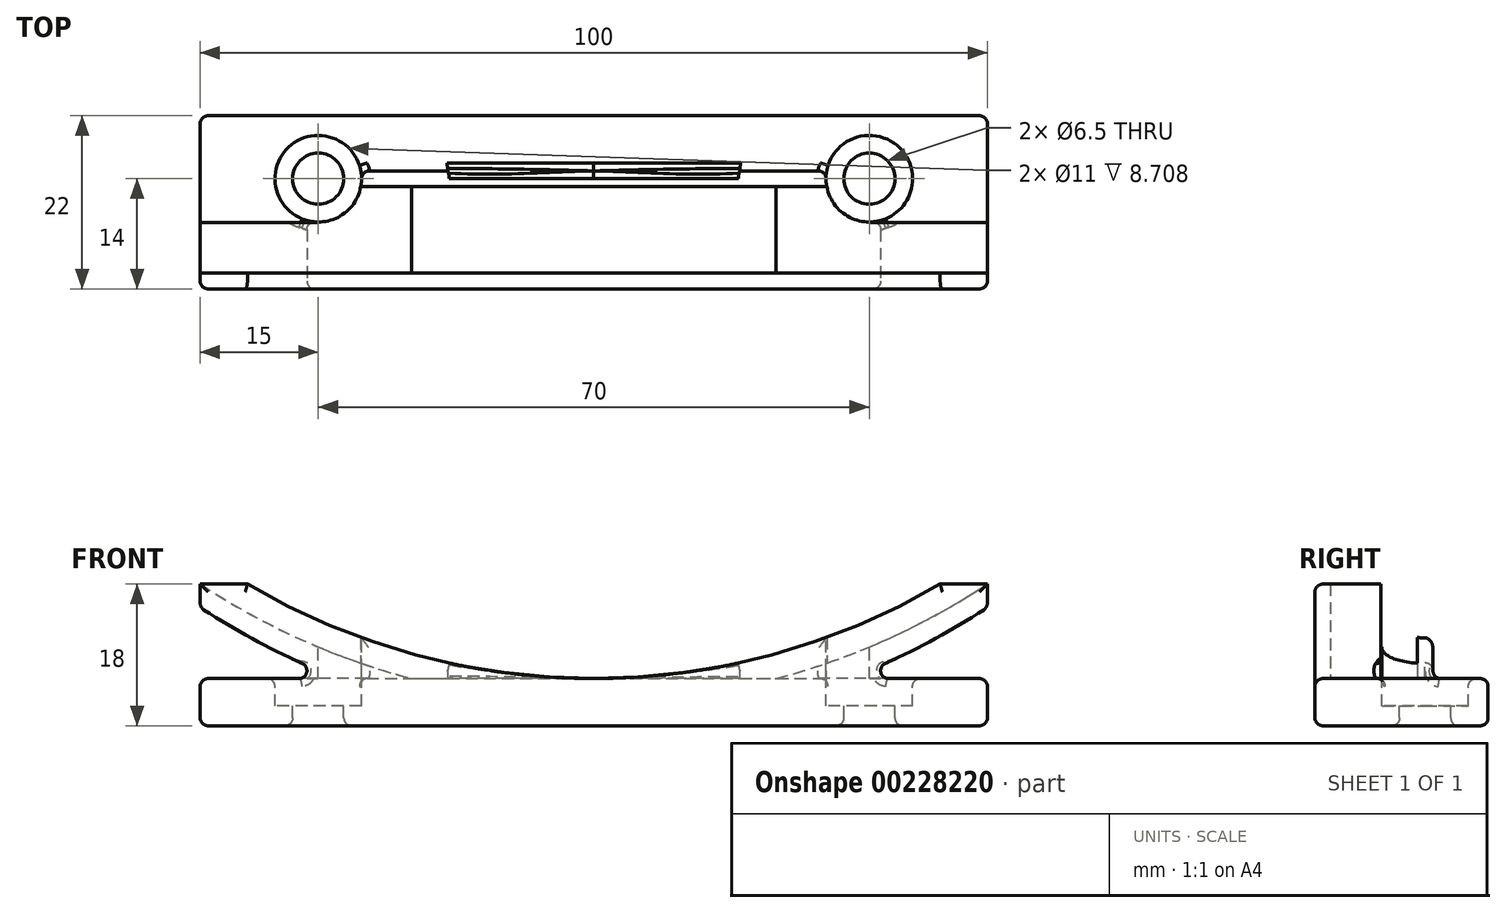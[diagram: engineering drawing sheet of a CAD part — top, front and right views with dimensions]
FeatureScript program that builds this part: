
annotation { "Feature Type Name" : "Feature", "Feature Type Description" : "" }
export const myFeature = defineFeature(function(context is Context, id is Id, definition is map)
    precondition{}
    {
        {
            var Q0;
            Q0=qCreatedBy(makeId("Top.planeOp"),FACE);
            var sketch = newSketch(context, id + "F0", { "sketchPlane" : qUnion([Q0])});
            skLineSegment(sketch, "E0.bottom", {"start": v(-50, 11) * mm, "end": v(50, 11) * mm});
            skLineSegment(sketch, "E0.top", {"start": v(-50, -11) * mm, "end": v(50, -11) * mm});
            skLineSegment(sketch, "E0.left", {"start": v(-50, 11) * mm, "end": v(-50, -11) * mm});
            skLineSegment(sketch, "E0.right", {"start": v(50, 11) * mm, "end": v(50, -11) * mm});
            skPoint(sketch, "E0.middle", {"position": v(0, 0) * mm});
            skSolve(sketch);
        }
        {
            var Q0;
            Q0=makeQuery(id+"F0.imprint","IMPRINT",FACE,{"disambiguationData":[TD([[makeQuery(id+"F0.imprint","IMPRINT",EDGE,{"derivedFrom":sQuery(id+"F0.wireOp",EDGE,"E0.bottom")}),-1.0]])]});
            extrude(context, id + "F1", {"entities" : qUnion([Q0]), "depth" : 6 * mm});
        }
        {
            var Q0;
            Q0=makeQuery(id+"F1.opExtrude","CAP_FACE",FACE,{"disambiguationData":[OSD([sQuery(id+"F0.wireOp",EDGE,"E0.bottom"),sQuery(id+"F0.wireOp",EDGE,"E0.top"),sQuery(id+"F0.wireOp",EDGE,"E0.left"),sQuery(id+"F0.wireOp",EDGE,"E0.right")])],"isStart":false});
            var sketch = newSketch(context, id + "F2", { "sketchPlane" : qUnion([Q0])});
            skPoint(sketch, "E1", {"position": v(35, 3) * mm});
            skPoint(sketch, "E2", {"position": v(-35, 3) * mm});
            skPoint(sketch, "E3", {"position": v(0, 3) * mm});
            skSolve(sketch);
        }
        {
            var Q0;
            Q0=sQuery(id+"F2.wireOp",VERTEX,"E2");
            var Q1;
            Q1=sQuery(id+"F2.wireOp",VERTEX,"E1");
            var Q2;
            Q2=makeQuery(id+"F1.opExtrude","SWEPT_BODY",BODY,{"disambiguationData":[OSD([sQuery(id+"F0.wireOp",EDGE,"E0.bottom"),sQuery(id+"F0.wireOp",EDGE,"E0.top"),sQuery(id+"F0.wireOp",EDGE,"E0.left"),sQuery(id+"F0.wireOp",EDGE,"E0.right")])]});
            hole(context, id + "F3", {"style" : HoleStyle.C_BORE, "endStyle" : HoleEndStyle.THROUGH, "holeDiameter" : 6.5 * mm, "cBoreDiameter" : 11 * mm, "cBoreDepth" : 3.5 * mm, "startFromSketch" : true, "locations" : qUnion([Q0, Q1]), "scope" : qUnion([Q2]), "isTappedThrough" : true});
        }
        {
            var Q0;
            Q0=makeQuery(id+"F1.opExtrude","SWEPT_FACE",FACE,{"disambiguationData":[OSD([sQuery(id+"F0.wireOp",EDGE,"E0.top")])]});
            var sketch = newSketch(context, id + "F4", { "sketchPlane" : qUnion([Q0])});
            skLineSegment(sketch, "E4.bottom", {"start": v(-50, 0) * mm, "end": v(50, 0) * mm});
            skLineSegment(sketch, "E4.top", {"start": v(-50, 18) * mm, "end": v(50, 18) * mm});
            skLineSegment(sketch, "E4.left", {"start": v(-50, 0) * mm, "end": v(-50, 18) * mm});
            skLineSegment(sketch, "E4.right", {"start": v(50, 0) * mm, "end": v(50, 18) * mm});
            skPoint(sketch, "E5", {"position": v(0, 3) * mm});
            skArc(sketch, "E6", {"start": v(-50, 18) * mm, "mid": v(0, 3) * mm, "end": v(50, 18) * mm});
            skArc(sketch, "E7", {"start": v(-44, 18) * mm, "mid": v(0, 6) * mm, "end": v(44, 18) * mm});
            skPoint(sketch, "E8", {"position": v(-50, 15.04) * mm});
            skPoint(sketch, "E9", {"position": v(50, 15.04) * mm});
            skArc(sketch, "E10", {"start": v(-50, 15.04) * mm, "mid": v(0, 0) * mm, "end": v(50, 15.04) * mm});
            skSolve(sketch);
        }
        {
            var Q0;
            {var subQ1=sQuery(id+"F4.wireOp",EDGE,"E4.top");var subQ3=sQuery(id+"F4.wireOp",EDGE,"E7");var subQ4=makeQuery(id+"F4.imprint","INTERSECT",VERTEX,{"disambiguationData":[OD(0.0)],"derivedFrom":[subQ1,subQ3]});Q0=makeQuery(id+"F4.imprint","IMPRINT",FACE,{"disambiguationData":[TD([[makeQuery(id+"F4.imprint","IMPRINT",EDGE,{"disambiguationData":[TD([[subQ4,-1.0]])],"derivedFrom":subQ3}),-1.0]])]});}
            var Q1;
            {var subQ1=sQuery(id+"F4.wireOp",EDGE,"E4.top");var subQ3=sQuery(id+"F4.wireOp",EDGE,"E7");var subQ4=makeQuery(id+"F4.imprint","INTERSECT",VERTEX,{"disambiguationData":[OD(1.0)],"derivedFrom":[subQ1,subQ3]});Q1=makeQuery(id+"F4.imprint","IMPRINT",FACE,{"disambiguationData":[TD([[makeQuery(id+"F4.imprint","IMPRINT",EDGE,{"disambiguationData":[TD([[subQ4,1.0]])],"derivedFrom":subQ3}),-1.0]])]});}
            var Q2;
            {var subQ1=sQuery(id+"F4.wireOp",EDGE,"E4.left");var subQ3=sQuery(id+"F4.wireOp",EDGE,"E10");var subQ4=makeQuery(id+"F4.imprint","INTERSECT",VERTEX,{"derivedFrom":[subQ1,subQ3]});Q2=makeQuery(id+"F4.imprint","IMPRINT",FACE,{"disambiguationData":[TD([[makeQuery(id+"F4.imprint","IMPRINT",EDGE,{"disambiguationData":[TD([[subQ4,-1.0]])],"derivedFrom":subQ3}),1.0]])]});}
            var Q3;
            {var subQ1=sQuery(id+"F4.wireOp",EDGE,"E4.right");var subQ3=sQuery(id+"F4.wireOp",EDGE,"E10");var subQ4=makeQuery(id+"F4.imprint","INTERSECT",VERTEX,{"derivedFrom":[subQ1,subQ3]});Q3=makeQuery(id+"F4.imprint","IMPRINT",FACE,{"disambiguationData":[TD([[makeQuery(id+"F4.imprint","IMPRINT",EDGE,{"disambiguationData":[TD([[subQ4,1.0]])],"derivedFrom":subQ3}),1.0]])]});}
            extrude(context, id + "F5", {"entities" : qUnion([Q0, Q1, Q2, Q3]), "operationType" : NewBodyOperationType.ADD, "oppositeDirection" : true, "depth" : 15 * mm});
        }
        {
            var Q0;
            {var subQ1=sQuery(id+"F4.wireOp",EDGE,"E4.top");var subQ3=sQuery(id+"F4.wireOp",EDGE,"E7");var subQ4=makeQuery(id+"F4.imprint","INTERSECT",VERTEX,{"disambiguationData":[OD(0.0)],"derivedFrom":[subQ1,subQ3]});Q0=makeQuery(id+"F4.imprint","IMPRINT",FACE,{"disambiguationData":[TD([[makeQuery(id+"F4.imprint","IMPRINT",EDGE,{"disambiguationData":[TD([[subQ4,-1.0]])],"derivedFrom":subQ3}),-1.0]])]});}
            var Q1;
            {var subQ0=sQuery(id+"F4.wireOp",EDGE,"E6");var subQ1=makeQuery(id+"F1.opExtrude","CAP_EDGE",EDGE,{"disambiguationData":[OSD([sQuery(id+"F0.wireOp",EDGE,"E0.top")])],"isStart":false});var subQ2=makeQuery(id+"F4.imprint","INTERSECT",VERTEX,{"disambiguationData":[OD(0.0)],"derivedFrom":[subQ1,subQ0]});Q1=makeQuery(id+"F4.imprint","IMPRINT",FACE,{"disambiguationData":[TD([[makeQuery(id+"F4.imprint","IMPRINT",EDGE,{"disambiguationData":[TD([[subQ2,-1.0]])],"derivedFrom":subQ0}),1.0]])]});}
            var Q2;
            {var subQ1=sQuery(id+"F4.wireOp",EDGE,"E4.top");var subQ3=sQuery(id+"F4.wireOp",EDGE,"E7");var subQ4=makeQuery(id+"F4.imprint","INTERSECT",VERTEX,{"disambiguationData":[OD(1.0)],"derivedFrom":[subQ1,subQ3]});Q2=makeQuery(id+"F4.imprint","IMPRINT",FACE,{"disambiguationData":[TD([[makeQuery(id+"F4.imprint","IMPRINT",EDGE,{"disambiguationData":[TD([[subQ4,1.0]])],"derivedFrom":subQ3}),-1.0]])]});}
            extrude(context, id + "F6", {"entities" : qUnion([Q0, Q1, Q2]), "operationType" : NewBodyOperationType.REMOVE, "oppositeDirection" : true, "depth" : 13 * mm, "hasSecondDirection" : true, "secondDirectionOppositeDirection" : true, "secondDirectionDepth" : 2 * mm});
        }
        {
            var Q0;
            Q0=sQuery(id+"F2.wireOp",VERTEX,"E2");
            var Q1;
            Q1=sQuery(id+"F2.wireOp",VERTEX,"E1");
            var Q2;
            Q2=makeQuery(id+"F1.opExtrude","SWEPT_BODY",BODY,{"disambiguationData":[OSD([sQuery(id+"F0.wireOp",EDGE,"E0.bottom"),sQuery(id+"F0.wireOp",EDGE,"E0.top"),sQuery(id+"F0.wireOp",EDGE,"E0.left"),sQuery(id+"F0.wireOp",EDGE,"E0.right")])]});
            hole(context, id + "F7", {"style" : HoleStyle.SIMPLE, "endStyle" : HoleEndStyle.THROUGH, "oppositeDirection" : true, "holeDiameter" : 11 * mm, "startFromSketch" : true, "locations" : qUnion([Q0, Q1]), "scope" : qUnion([Q2]), "isTappedThrough" : true});
        }
        {
            var Q0;
            {var subQ0=sQuery(id+"F4.wireOp",EDGE,"E10");var subQ1=sQuery(id+"F4.wireOp",EDGE,"E7");var subQ2=sQuery(id+"F4.wireOp",EDGE,"E4.top");var subQ3=sQuery(id+"F0.wireOp",EDGE,"E0.top");Q0=makeQuery(id+"F5.boolean.opBoolean","MERGE",FACE,{"derivedFrom":[makeQuery(id+"F1.opExtrude","SWEPT_FACE",FACE,{"disambiguationData":[OSD([subQ3])]}),makeQuery(id+"F5.opExtrude","CAP_FACE",FACE,{"disambiguationData":[OSD([subQ3,subQ2,sQuery(id+"F4.wireOp",EDGE,"E4.left"),subQ1,subQ0])],"isStart":true}),makeQuery(id+"F5.opExtrude","CAP_FACE",FACE,{"disambiguationData":[OSD([subQ3,subQ2,sQuery(id+"F4.wireOp",EDGE,"E4.right"),subQ1,subQ0])],"isStart":true})]});}
            var Q1;
            {var subQ0=sQuery(id+"F4.wireOp",EDGE,"E10");Q1=makeQuery(id+"F5.opExtrude","SWEPT_FACE",FACE,{"disambiguationData":[OSD([subQ0]),TDD([makeQuery(id+"F4.imprint","IMPRINT",EDGE,{"disambiguationData":[TD([[makeQuery(id+"F4.imprint","INTERSECT",VERTEX,{"derivedFrom":[sQuery(id+"F4.wireOp",EDGE,"E4.left"),subQ0]}),-1.0]])],"derivedFrom":subQ0})])]});}
            var Q2;
            Q2=makeQuery(id+"F1.opExtrude","SWEPT_FACE",FACE,{"disambiguationData":[OSD([sQuery(id+"F0.wireOp",EDGE,"E0.left")])]});
            var Q3;
            Q3=makeQuery(id+"F1.opExtrude","CAP_FACE",FACE,{"disambiguationData":[OSD([sQuery(id+"F0.wireOp",EDGE,"E0.bottom"),sQuery(id+"F0.wireOp",EDGE,"E0.top"),sQuery(id+"F0.wireOp",EDGE,"E0.left"),sQuery(id+"F0.wireOp",EDGE,"E0.right")])],"isStart":true});
            var Q4;
            Q4=makeQuery(id+"F1.opExtrude","SWEPT_FACE",FACE,{"disambiguationData":[OSD([sQuery(id+"F0.wireOp",EDGE,"E0.bottom")])]});
            var Q5;
            Q5=makeQuery(id+"F1.opExtrude","SWEPT_FACE",FACE,{"disambiguationData":[OSD([sQuery(id+"F0.wireOp",EDGE,"E0.right")])]});
            var Q6;
            Q6=makeQuery(id+"F1.opExtrude","CAP_FACE",FACE,{"disambiguationData":[OSD([sQuery(id+"F0.wireOp",EDGE,"E0.bottom"),sQuery(id+"F0.wireOp",EDGE,"E0.top"),sQuery(id+"F0.wireOp",EDGE,"E0.left"),sQuery(id+"F0.wireOp",EDGE,"E0.right")])],"isStart":false});
            var Q7;
            {var subQ0=sQuery(id+"F4.wireOp",EDGE,"E10");Q7=makeQuery(id+"F5.opExtrude","SWEPT_FACE",FACE,{"disambiguationData":[OSD([subQ0]),TDD([makeQuery(id+"F4.imprint","IMPRINT",EDGE,{"disambiguationData":[TD([[makeQuery(id+"F4.imprint","INTERSECT",VERTEX,{"derivedFrom":[sQuery(id+"F4.wireOp",EDGE,"E4.right"),subQ0]}),1.0]])],"derivedFrom":subQ0})])]});}
            var Q8;
            {var subQ0=sQuery(id+"F4.wireOp",EDGE,"E4.right");var subQ1=sQuery(id+"F4.wireOp",EDGE,"E7");var subQ2=sQuery(id+"F4.wireOp",EDGE,"E4.top");var subQ4=sQuery(id+"F0.wireOp",EDGE,"E0.top");var subQ7=sQuery(id+"F4.wireOp",EDGE,"E10");Q8=makeQuery(id+"F7.hole-1.boolean.opBoolean","SPLIT",FACE,{"disambiguationData":[TD([makeQuery(id+"F5.opExtrude","SWEPT_FACE",FACE,{"disambiguationData":[OSD([subQ0])]})])],"derivedFrom":makeQuery(id+"F5.opExtrude","CAP_FACE",FACE,{"disambiguationData":[OSD([subQ4,subQ2,subQ0,subQ1,subQ7])],"isStart":false})});}
            var Q9;
            {var subQ0=sQuery(id+"F4.wireOp",EDGE,"E4.left");var subQ1=sQuery(id+"F4.wireOp",EDGE,"E7");var subQ2=sQuery(id+"F4.wireOp",EDGE,"E4.top");var subQ4=sQuery(id+"F0.wireOp",EDGE,"E0.top");var subQ7=sQuery(id+"F4.wireOp",EDGE,"E10");Q9=makeQuery(id+"F7.hole-0.boolean.opBoolean","SPLIT",FACE,{"disambiguationData":[TD([makeQuery(id+"F5.opExtrude","SWEPT_FACE",FACE,{"disambiguationData":[OSD([subQ0])]})])],"derivedFrom":makeQuery(id+"F5.opExtrude","CAP_FACE",FACE,{"disambiguationData":[OSD([subQ4,subQ2,subQ0,subQ1,subQ7])],"isStart":false})});}
            var Q10;
            {var subQ0=sQuery(id+"F4.wireOp",EDGE,"E7");var subQ1=sQuery(id+"F4.wireOp",EDGE,"E4.top");var subQ2=makeQuery(id+"F4.imprint","INTERSECT",VERTEX,{"disambiguationData":[OD(1.0)],"derivedFrom":[subQ1,subQ0]});var subQ8=makeQuery(id+"F3.hole-0.boolean.opBoolean","COPY",FACE,{"derivedFrom":makeQuery(id+"F3.hole-0.opRevolve","SWEPT_FACE",FACE,{"disambiguationData":[OSD([sQuery(id+"F3.hole-0.sketch.wireOp",EDGE,"cbore_start_line_2")])]})});Q10=makeQuery(id+"F7.hole-1.boolean.opBoolean","SPLIT",EDGE,{"disambiguationData":[TD([subQ8])],"derivedFrom":makeQuery(id+"F7.hole-0.boolean.opBoolean","SPLIT",EDGE,{"disambiguationData":[TD([makeQuery(id+"F5.opExtrude","SWEPT_FACE",FACE,{"disambiguationData":[OSD([subQ1]),TDD([makeQuery(id+"F4.imprint","IMPRINT",EDGE,{"disambiguationData":[TD([[subQ2,-1.0]])],"derivedFrom":subQ1})])]})])],"derivedFrom":makeQuery(id+"F6.boolean.opBoolean","COPY",EDGE,{"derivedFrom":makeQuery(id+"F6.opExtrude","CAP_EDGE",EDGE,{"disambiguationData":[OSD([subQ0])],"isStart":false})})})});}
            var Q11;
            {var subQ0=sQuery(id+"F4.wireOp",EDGE,"E4.right");var subQ1=sQuery(id+"F4.wireOp",EDGE,"E7");var subQ2=sQuery(id+"F4.wireOp",EDGE,"E4.top");var subQ5=sQuery(id+"F4.wireOp",EDGE,"E6");Q11=makeQuery(id+"F7.hole-1.boolean.opBoolean","INTERSECT",EDGE,{"disambiguationData":[OD(0.0)],"derivedFrom":[makeQuery(id+"F7.hole-0.boolean.opBoolean","SPLIT",FACE,{"disambiguationData":[TD([makeQuery(id+"F5.opExtrude","SWEPT_FACE",FACE,{"disambiguationData":[OSD([subQ0])]})])],"derivedFrom":makeQuery(id+"F6.boolean.opBoolean","COPY",FACE,{"derivedFrom":makeQuery(id+"F6.opExtrude","CAP_FACE",FACE,{"disambiguationData":[OSD([subQ2,subQ5,subQ1])],"isStart":false})})}),makeQuery(id+"F7.hole-1.opRevolve","SWEPT_FACE",FACE,{"disambiguationData":[OSD([sQuery(id+"F7.hole-1.sketch.wireOp",EDGE,"core_line_2")])]})]});}
            var Q12;
            {var subQ0=sQuery(id+"F4.wireOp",EDGE,"E4.top");Q12=makeQuery(id+"F6.boolean.opBoolean","COPY",EDGE,{"derivedFrom":makeQuery(id+"F6.opExtrude","CAP_EDGE",EDGE,{"disambiguationData":[OSD([subQ0]),TDD([makeQuery(id+"F4.imprint","IMPRINT",EDGE,{"disambiguationData":[TD([[makeQuery(id+"F4.imprint","INTERSECT",VERTEX,{"disambiguationData":[OD(1.0)],"derivedFrom":[subQ0,sQuery(id+"F4.wireOp",EDGE,"E7")]}),-1.0]])],"derivedFrom":subQ0})])],"isStart":false})});}
            var Q13;
            {var subQ0=sQuery(id+"F4.wireOp",EDGE,"E7");var subQ1=sQuery(id+"F4.wireOp",EDGE,"E4.top");var subQ2=makeQuery(id+"F4.imprint","INTERSECT",VERTEX,{"disambiguationData":[OD(1.0)],"derivedFrom":[subQ1,subQ0]});var subQ7=makeQuery(id+"F5.opExtrude","SWEPT_FACE",FACE,{"disambiguationData":[OSD([subQ1]),TDD([makeQuery(id+"F4.imprint","IMPRINT",EDGE,{"disambiguationData":[TD([[subQ2,-1.0]])],"derivedFrom":subQ1})])]});Q13=makeQuery(id+"F7.hole-1.boolean.opBoolean","SPLIT",EDGE,{"disambiguationData":[TD([subQ7])],"derivedFrom":makeQuery(id+"F7.hole-0.boolean.opBoolean","SPLIT",EDGE,{"disambiguationData":[TD([subQ7])],"derivedFrom":makeQuery(id+"F6.boolean.opBoolean","COPY",EDGE,{"derivedFrom":makeQuery(id+"F6.opExtrude","CAP_EDGE",EDGE,{"disambiguationData":[OSD([subQ0])],"isStart":false})})})});}
            var Q14;
            {var subQ0=sQuery(id+"F4.wireOp",EDGE,"E4.top");Q14=makeQuery(id+"F6.boolean.opBoolean","COPY",EDGE,{"derivedFrom":makeQuery(id+"F6.opExtrude","CAP_EDGE",EDGE,{"disambiguationData":[OSD([subQ0]),TDD([makeQuery(id+"F4.imprint","IMPRINT",EDGE,{"disambiguationData":[TD([[makeQuery(id+"F4.imprint","INTERSECT",VERTEX,{"disambiguationData":[OD(0.0)],"derivedFrom":[subQ0,sQuery(id+"F4.wireOp",EDGE,"E7")]}),1.0]])],"derivedFrom":subQ0})])],"isStart":false})});}
            var Q15;
            {var subQ0=sQuery(id+"F4.wireOp",EDGE,"E7");var subQ1=sQuery(id+"F4.wireOp",EDGE,"E4.top");var subQ3=makeQuery(id+"F4.imprint","INTERSECT",VERTEX,{"disambiguationData":[OD(0.0)],"derivedFrom":[subQ1,subQ0]});Q15=makeQuery(id+"F7.hole-0.boolean.opBoolean","SPLIT",EDGE,{"disambiguationData":[TD([makeQuery(id+"F5.opExtrude","SWEPT_FACE",FACE,{"disambiguationData":[OSD([subQ1]),TDD([makeQuery(id+"F4.imprint","IMPRINT",EDGE,{"disambiguationData":[TD([[subQ3,1.0]])],"derivedFrom":subQ1})])]})])],"derivedFrom":makeQuery(id+"F6.boolean.opBoolean","COPY",EDGE,{"derivedFrom":makeQuery(id+"F6.opExtrude","CAP_EDGE",EDGE,{"disambiguationData":[OSD([subQ0])],"isStart":false})})});}
            var Q16;
            Q16=makeQuery(id+"F7.hole-0.boolean.opBoolean","INTERSECT",EDGE,{"disambiguationData":[OD(0.0)],"derivedFrom":[makeQuery(id+"F6.boolean.opBoolean","COPY",FACE,{"derivedFrom":makeQuery(id+"F6.opExtrude","CAP_FACE",FACE,{"disambiguationData":[OSD([sQuery(id+"F4.wireOp",EDGE,"E4.top"),sQuery(id+"F4.wireOp",EDGE,"E6"),sQuery(id+"F4.wireOp",EDGE,"E7")])],"isStart":false})}),makeQuery(id+"F7.hole-0.opRevolve","SWEPT_FACE",FACE,{"disambiguationData":[OSD([sQuery(id+"F7.hole-0.sketch.wireOp",EDGE,"core_line_2")])]})]});
            var Q17;
            {var subQ0=sQuery(id+"F4.wireOp",EDGE,"E4.top");Q17=makeQuery(id+"F6.boolean.opBoolean","COPY",EDGE,{"derivedFrom":makeQuery(id+"F6.opExtrude","CAP_EDGE",EDGE,{"disambiguationData":[OSD([subQ0]),TDD([makeQuery(id+"F4.imprint","IMPRINT",EDGE,{"disambiguationData":[TD([[makeQuery(id+"F4.imprint","INTERSECT",VERTEX,{"disambiguationData":[OD(1.0)],"derivedFrom":[subQ0,sQuery(id+"F4.wireOp",EDGE,"E7")]}),-1.0]])],"derivedFrom":subQ0})])],"isStart":true})});}
            var Q18;
            Q18=makeQuery(id+"F6.boolean.opBoolean","COPY",EDGE,{"derivedFrom":makeQuery(id+"F6.opExtrude","CAP_EDGE",EDGE,{"disambiguationData":[OSD([sQuery(id+"F4.wireOp",EDGE,"E7")])],"isStart":true})});
            var Q19;
            {var subQ0=sQuery(id+"F4.wireOp",EDGE,"E4.top");Q19=makeQuery(id+"F6.boolean.opBoolean","COPY",EDGE,{"derivedFrom":makeQuery(id+"F6.opExtrude","CAP_EDGE",EDGE,{"disambiguationData":[OSD([subQ0]),TDD([makeQuery(id+"F4.imprint","IMPRINT",EDGE,{"disambiguationData":[TD([[makeQuery(id+"F4.imprint","INTERSECT",VERTEX,{"disambiguationData":[OD(0.0)],"derivedFrom":[subQ0,sQuery(id+"F4.wireOp",EDGE,"E7")]}),1.0]])],"derivedFrom":subQ0})])],"isStart":true})});}
            fillet(context, id + "F8", {"entities" : qUnion([Q0, Q1, Q2, Q3, Q4, Q5, Q6, Q7, Q8, Q9, Q10, Q11, Q12, Q13, Q14, Q15, Q16, Q17, Q18, Q19]), "radius" : 1 * mm, "tangentPropagation" : true, "allowEdgeOverflow" : false});
        }
        {
            var Q0;
            Q0=qCreatedBy(makeId("Front.planeOp"),FACE);
            var sketch = newSketch(context, id + "F9", { "sketchPlane" : qUnion([Q0])});
            skLineSegment(sketch, "E11.bottom", {"start": v(53, 21.33) * mm, "end": v(35, 21.33) * mm});
            skLineSegment(sketch, "E11.top", {"start": v(53, 6) * mm, "end": v(35, 6) * mm});
            skLineSegment(sketch, "E11.left", {"start": v(53, 21.33) * mm, "end": v(53, 6) * mm});
            skLineSegment(sketch, "E11.right", {"start": v(35, 21.33) * mm, "end": v(35, 6) * mm});
            skLineSegment(sketch, "E12.bottom", {"start": v(-53, 19.33) * mm, "end": v(-35, 19.33) * mm});
            skLineSegment(sketch, "E12.top", {"start": v(-53, 6) * mm, "end": v(-35, 6) * mm});
            skLineSegment(sketch, "E12.left", {"start": v(-53, 19.33) * mm, "end": v(-53, 6) * mm});
            skLineSegment(sketch, "E12.right", {"start": v(-35, 19.33) * mm, "end": v(-35, 6) * mm});
            skSolve(sketch);
        }
        {
            var Q0;
            Q0=makeQuery(id+"F9.imprint","IMPRINT",FACE,{"disambiguationData":[TD([[makeQuery(id+"F9.imprint","IMPRINT",EDGE,{"derivedFrom":sQuery(id+"F9.wireOp",EDGE,"E11.bottom")}),1.0]])]});
            var Q1;
            Q1=makeQuery(id+"F9.imprint","IMPRINT",FACE,{"disambiguationData":[TD([[makeQuery(id+"F9.imprint","IMPRINT",EDGE,{"derivedFrom":sQuery(id+"F9.wireOp",EDGE,"E12.bottom")}),-1.0]])]});
            extrude(context, id + "F10", {"entities" : qUnion([Q0, Q1]), "operationType" : NewBodyOperationType.REMOVE, "oppositeDirection" : true, "depth" : 25 * mm, "hasSecondDirection" : true, "secondDirectionOppositeDirection" : false, "secondDirectionDepth" : 2.6 * mm});
        }
    });
